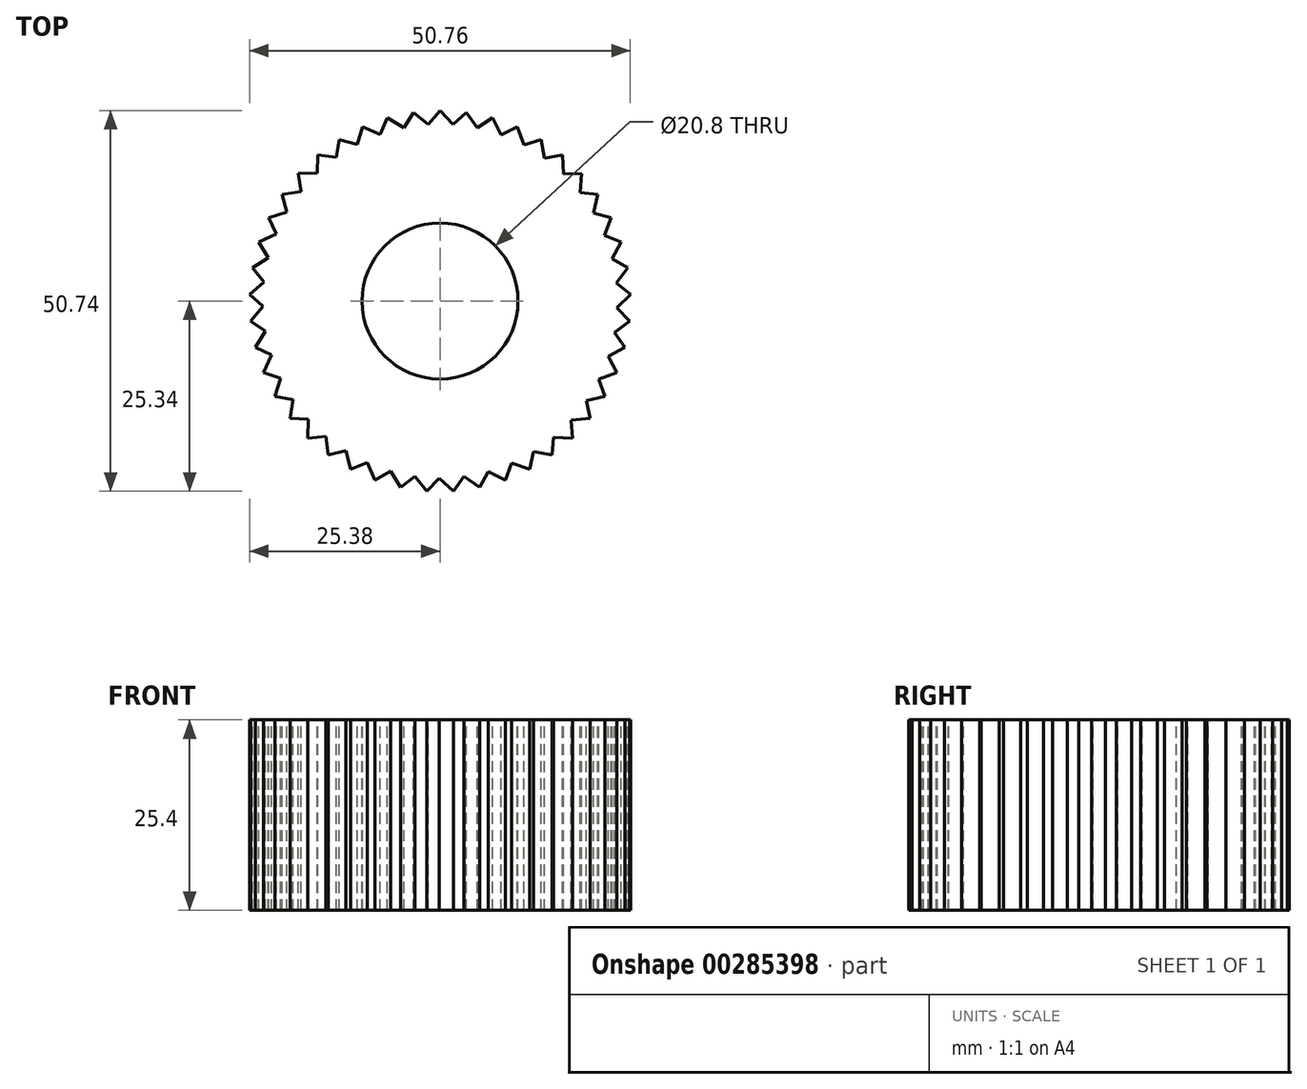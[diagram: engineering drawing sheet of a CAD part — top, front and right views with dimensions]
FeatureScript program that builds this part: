
annotation { "Feature Type Name" : "Feature", "Feature Type Description" : "" }
export const myFeature = defineFeature(function(context is Context, id is Id, definition is map)
    precondition{}
    {
        {
            var Q0;
            Q0=qCreatedBy(makeId("Top.planeOp"),FACE);
            var sketch = newSketch(context, id + "F0", { "sketchPlane" : qUnion([Q0])});
            skCircle(sketch, "E0", {"center": v(0, 0) * mm, "radius": 25.4 * mm});
            skSolve(sketch);
        }
        {
            var Q0;
            Q0=makeQuery(id+"F0.imprint","IMPRINT",FACE,{"disambiguationData":[TD([[makeQuery(id+"F0.imprint","IMPRINT",EDGE,{"derivedFrom":sQuery(id+"F0.wireOp",EDGE,"E0")}),1.0]])]});
            extrude(context, id + "F1", {"entities" : qUnion([Q0]), "depth" : 25.4 * mm});
        }
        {
            var Q0;
            Q0=makeQuery(id+"F1.opExtrude","CAP_FACE",FACE,{"disambiguationData":[OSD([sQuery(id+"F0.wireOp",EDGE,"E0")])],"isStart":false});
            var sketch = newSketch(context, id + "F2", { "sketchPlane" : qUnion([Q0])});
            skLineSegment(sketch, "E1", {"start": v(0, 0) * mm, "end": v(0, 49.68) * mm});
            skLineSegment(sketch, "E2", {"start": v(0, 24.84) * mm, "end": v(0, 25.4) * mm});
            skLineSegment(sketch, "E3", {"start": v(0, 25.4) * mm, "end": v(2.47, 22.76) * mm});
            skLineSegment(sketch, "E4", {"start": v(2.47, 22.76) * mm, "end": v(-2.23, 22.76) * mm});
            skLineSegment(sketch, "E5", {"start": v(-2.23, 22.76) * mm, "end": v(0, 25.4) * mm});
            skCircle(sketch, "E6.0", {"center": v(0, 0) * mm, "radius": 25.4 * mm});
            skLineSegment(sketch, "E7.1.1", {"start": v(-3.53, 25.15) * mm, "end": v(-0.72, 22.88) * mm});
            skLineSegment(sketch, "E7.1.2", {"start": v(-0.72, 22.88) * mm, "end": v(-5.38, 22.23) * mm});
            skLineSegment(sketch, "E7.1.3", {"start": v(-5.38, 22.23) * mm, "end": v(-3.53, 25.15) * mm});
            skLineSegment(sketch, "E7.2.1", {"start": v(-7, 24.42) * mm, "end": v(-3.9, 22.56) * mm});
            skLineSegment(sketch, "E7.2.2", {"start": v(-3.9, 22.56) * mm, "end": v(-8.42, 21.26) * mm});
            skLineSegment(sketch, "E7.2.3", {"start": v(-8.42, 21.26) * mm, "end": v(-7, 24.42) * mm});
            skLineSegment(sketch, "E8.2.3.0", {"start": v(-10.33, 23.2) * mm, "end": v(-7, 21.8) * mm});
            skLineSegment(sketch, "E8.5.3.0", {"start": v(-7, 21.8) * mm, "end": v(-11.3, 19.88) * mm});
            skLineSegment(sketch, "E8.8.3.0", {"start": v(-11.3, 19.88) * mm, "end": v(-10.33, 23.2) * mm});
            skLineSegment(sketch, "E8.2.4.0", {"start": v(-13.46, 21.54) * mm, "end": v(-9.96, 20.6) * mm});
            skLineSegment(sketch, "E8.5.4.0", {"start": v(-9.96, 20.6) * mm, "end": v(-13.96, 18.12) * mm});
            skLineSegment(sketch, "E8.8.4.0", {"start": v(-13.96, 18.12) * mm, "end": v(-13.46, 21.54) * mm});
            skLineSegment(sketch, "E8.2.5.0", {"start": v(-16.33, 19.46) * mm, "end": v(-12.74, 19.02) * mm});
            skLineSegment(sketch, "E8.5.5.0", {"start": v(-12.74, 19.02) * mm, "end": v(-16.34, 16) * mm});
            skLineSegment(sketch, "E8.8.5.0", {"start": v(-16.34, 16) * mm, "end": v(-16.33, 19.46) * mm});
            skLineSegment(sketch, "E8.2.6.0", {"start": v(-18.88, 17) * mm, "end": v(-15.26, 17.06) * mm});
            skLineSegment(sketch, "E8.5.6.0", {"start": v(-15.26, 17.06) * mm, "end": v(-18.4, 13.57) * mm});
            skLineSegment(sketch, "E8.8.6.0", {"start": v(-18.4, 13.57) * mm, "end": v(-18.88, 17) * mm});
            skLineSegment(sketch, "E8.2.7.0", {"start": v(-21.06, 14.2) * mm, "end": v(-17.49, 14.78) * mm});
            skLineSegment(sketch, "E8.5.7.0", {"start": v(-17.49, 14.78) * mm, "end": v(-20.12, 10.87) * mm});
            skLineSegment(sketch, "E8.8.7.0", {"start": v(-20.12, 10.87) * mm, "end": v(-21.06, 14.2) * mm});
            skLineSegment(sketch, "E8.2.8.0", {"start": v(-22.83, 11.13) * mm, "end": v(-19.37, 12.2) * mm});
            skLineSegment(sketch, "E8.5.8.0", {"start": v(-19.37, 12.2) * mm, "end": v(-21.43, 7.97) * mm});
            skLineSegment(sketch, "E8.8.8.0", {"start": v(-21.43, 7.97) * mm, "end": v(-22.83, 11.13) * mm});
            skLineSegment(sketch, "E8.2.9.0", {"start": v(-24.16, 7.85) * mm, "end": v(-20.88, 9.38) * mm});
            skLineSegment(sketch, "E8.5.9.0", {"start": v(-20.88, 9.38) * mm, "end": v(-22.34, 4.9) * mm});
            skLineSegment(sketch, "E8.8.9.0", {"start": v(-22.34, 4.9) * mm, "end": v(-24.16, 7.85) * mm});
            skLineSegment(sketch, "E8.2.10.0", {"start": v(-25.01, 4.41) * mm, "end": v(-21.98, 6.39) * mm});
            skLineSegment(sketch, "E8.5.10.0", {"start": v(-21.98, 6.39) * mm, "end": v(-22.8, 1.75) * mm});
            skLineSegment(sketch, "E8.8.10.0", {"start": v(-22.8, 1.75) * mm, "end": v(-25.01, 4.41) * mm});
            skLineSegment(sketch, "E8.2.11.0", {"start": v(-25.38, 0.89) * mm, "end": v(-22.66, 3.26) * mm});
            skLineSegment(sketch, "E8.5.11.0", {"start": v(-22.66, 3.26) * mm, "end": v(-22.82, -1.44) * mm});
            skLineSegment(sketch, "E8.8.11.0", {"start": v(-22.82, -1.44) * mm, "end": v(-25.38, 0.89) * mm});
            skLineSegment(sketch, "E8.2.12.0", {"start": v(-25.26, -2.66) * mm, "end": v(-22.9, 0.08) * mm});
            skLineSegment(sketch, "E8.5.12.0", {"start": v(-22.9, 0.08) * mm, "end": v(-22.4, -4.6) * mm});
            skLineSegment(sketch, "E8.8.12.0", {"start": v(-22.4, -4.6) * mm, "end": v(-25.26, -2.66) * mm});
            skLineSegment(sketch, "E8.2.13.0", {"start": v(-24.65, -6.14) * mm, "end": v(-22.68, -3.1) * mm});
            skLineSegment(sketch, "E8.5.13.0", {"start": v(-22.68, -3.1) * mm, "end": v(-21.54, -7.67) * mm});
            skLineSegment(sketch, "E8.8.13.0", {"start": v(-21.54, -7.67) * mm, "end": v(-24.65, -6.14) * mm});
            skLineSegment(sketch, "E8.2.14.0", {"start": v(-23.55, -9.52) * mm, "end": v(-22.03, -6.23) * mm});
            skLineSegment(sketch, "E8.5.14.0", {"start": v(-22.03, -6.23) * mm, "end": v(-20.26, -10.6) * mm});
            skLineSegment(sketch, "E8.8.14.0", {"start": v(-20.26, -10.6) * mm, "end": v(-23.55, -9.52) * mm});
            skLineSegment(sketch, "E8.2.15.0", {"start": v(-22, -12.7) * mm, "end": v(-20.95, -9.24) * mm});
            skLineSegment(sketch, "E8.5.15.0", {"start": v(-20.95, -9.24) * mm, "end": v(-18.6, -13.31) * mm});
            skLineSegment(sketch, "E8.8.15.0", {"start": v(-18.6, -13.31) * mm, "end": v(-22, -12.7) * mm});
            skLineSegment(sketch, "E8.2.16.0", {"start": v(-20.02, -15.64) * mm, "end": v(-19.46, -12.06) * mm});
            skLineSegment(sketch, "E8.5.16.0", {"start": v(-19.46, -12.06) * mm, "end": v(-16.56, -15.77) * mm});
            skLineSegment(sketch, "E8.8.16.0", {"start": v(-16.56, -15.77) * mm, "end": v(-20.02, -15.64) * mm});
            skLineSegment(sketch, "E8.2.17.0", {"start": v(-17.64, -18.27) * mm, "end": v(-17.59, -14.65) * mm});
            skLineSegment(sketch, "E8.5.17.0", {"start": v(-17.59, -14.65) * mm, "end": v(-14.2, -17.92) * mm});
            skLineSegment(sketch, "E8.8.17.0", {"start": v(-14.2, -17.92) * mm, "end": v(-17.64, -18.27) * mm});
            skLineSegment(sketch, "E8.2.18.0", {"start": v(-14.93, -20.55) * mm, "end": v(-15.38, -16.96) * mm});
            skLineSegment(sketch, "E8.5.18.0", {"start": v(-15.38, -16.96) * mm, "end": v(-11.57, -19.73) * mm});
            skLineSegment(sketch, "E8.8.18.0", {"start": v(-11.57, -19.73) * mm, "end": v(-14.93, -20.55) * mm});
            skLineSegment(sketch, "E8.2.19.0", {"start": v(-11.92, -22.43) * mm, "end": v(-12.87, -18.93) * mm});
            skLineSegment(sketch, "E8.5.19.0", {"start": v(-12.87, -18.93) * mm, "end": v(-8.71, -21.14) * mm});
            skLineSegment(sketch, "E8.8.19.0", {"start": v(-8.71, -21.14) * mm, "end": v(-11.92, -22.43) * mm});
            skLineSegment(sketch, "E8.2.20.0", {"start": v(-8.69, -23.87) * mm, "end": v(-10.1, -20.54) * mm});
            skLineSegment(sketch, "E8.5.20.0", {"start": v(-10.1, -20.54) * mm, "end": v(-5.68, -22.15) * mm});
            skLineSegment(sketch, "E8.8.20.0", {"start": v(-5.68, -22.15) * mm, "end": v(-8.69, -23.87) * mm});
            skLineSegment(sketch, "E8.2.21.0", {"start": v(-5.28, -24.84) * mm, "end": v(-7.15, -21.75) * mm});
            skLineSegment(sketch, "E8.5.21.0", {"start": v(-7.15, -21.75) * mm, "end": v(-2.55, -22.73) * mm});
            skLineSegment(sketch, "E8.8.21.0", {"start": v(-2.55, -22.73) * mm, "end": v(-5.28, -24.84) * mm});
            skLineSegment(sketch, "E8.2.22.0", {"start": v(-1.77, -25.34) * mm, "end": v(-4.05, -22.53) * mm});
            skLineSegment(sketch, "E8.5.22.0", {"start": v(-4.05, -22.53) * mm, "end": v(0.64, -22.86) * mm});
            skLineSegment(sketch, "E8.8.22.0", {"start": v(0.64, -22.86) * mm, "end": v(-1.77, -25.34) * mm});
            skLineSegment(sketch, "E8.2.23.0", {"start": v(1.77, -25.34) * mm, "end": v(-0.88, -22.88) * mm});
            skLineSegment(sketch, "E8.5.23.0", {"start": v(-0.88, -22.88) * mm, "end": v(3.82, -22.55) * mm});
            skLineSegment(sketch, "E8.8.23.0", {"start": v(3.82, -22.55) * mm, "end": v(1.77, -25.34) * mm});
            skLineSegment(sketch, "E8.2.24.0", {"start": v(5.28, -24.84) * mm, "end": v(2.31, -22.78) * mm});
            skLineSegment(sketch, "E8.5.24.0", {"start": v(2.31, -22.78) * mm, "end": v(6.92, -21.8) * mm});
            skLineSegment(sketch, "E8.8.24.0", {"start": v(6.92, -21.8) * mm, "end": v(5.28, -24.84) * mm});
            skLineSegment(sketch, "E8.2.25.0", {"start": v(8.69, -23.87) * mm, "end": v(5.46, -22.23) * mm});
            skLineSegment(sketch, "E8.5.25.0", {"start": v(5.46, -22.23) * mm, "end": v(9.88, -20.62) * mm});
            skLineSegment(sketch, "E8.8.25.0", {"start": v(9.88, -20.62) * mm, "end": v(8.69, -23.87) * mm});
            skLineSegment(sketch, "E8.2.26.0", {"start": v(11.92, -22.43) * mm, "end": v(8.5, -21.25) * mm});
            skLineSegment(sketch, "E8.5.26.0", {"start": v(8.5, -21.25) * mm, "end": v(12.66, -19.05) * mm});
            skLineSegment(sketch, "E8.8.26.0", {"start": v(12.66, -19.05) * mm, "end": v(11.92, -22.43) * mm});
            skLineSegment(sketch, "E8.2.27.0", {"start": v(14.93, -20.55) * mm, "end": v(11.38, -19.86) * mm});
            skLineSegment(sketch, "E8.5.27.0", {"start": v(11.38, -19.86) * mm, "end": v(15.19, -17.1) * mm});
            skLineSegment(sketch, "E8.8.27.0", {"start": v(15.19, -17.1) * mm, "end": v(14.93, -20.55) * mm});
            skLineSegment(sketch, "E8.2.28.0", {"start": v(17.64, -18.27) * mm, "end": v(14.03, -18.09) * mm});
            skLineSegment(sketch, "E8.5.28.0", {"start": v(14.03, -18.09) * mm, "end": v(17.42, -14.82) * mm});
            skLineSegment(sketch, "E8.8.28.0", {"start": v(17.42, -14.82) * mm, "end": v(17.64, -18.27) * mm});
            skLineSegment(sketch, "E8.2.29.0", {"start": v(20.02, -15.64) * mm, "end": v(16.41, -15.96) * mm});
            skLineSegment(sketch, "E8.5.29.0", {"start": v(16.41, -15.96) * mm, "end": v(19.3, -12.25) * mm});
            skLineSegment(sketch, "E8.8.29.0", {"start": v(19.3, -12.25) * mm, "end": v(20.02, -15.64) * mm});
            skLineSegment(sketch, "E8.2.30.0", {"start": v(22, -12.7) * mm, "end": v(18.47, -13.52) * mm});
            skLineSegment(sketch, "E8.5.30.0", {"start": v(18.47, -13.52) * mm, "end": v(20.83, -9.44) * mm});
            skLineSegment(sketch, "E8.8.30.0", {"start": v(20.83, -9.44) * mm, "end": v(22, -12.7) * mm});
            skLineSegment(sketch, "E8.2.31.0", {"start": v(23.55, -9.52) * mm, "end": v(20.18, -10.82) * mm});
            skLineSegment(sketch, "E8.5.31.0", {"start": v(20.18, -10.82) * mm, "end": v(21.94, -6.45) * mm});
            skLineSegment(sketch, "E8.8.31.0", {"start": v(21.94, -6.45) * mm, "end": v(23.55, -9.52) * mm});
            skLineSegment(sketch, "E8.2.32.0", {"start": v(24.65, -6.14) * mm, "end": v(21.48, -7.9) * mm});
            skLineSegment(sketch, "E8.5.32.0", {"start": v(21.48, -7.9) * mm, "end": v(22.62, -3.34) * mm});
            skLineSegment(sketch, "E8.8.32.0", {"start": v(22.62, -3.34) * mm, "end": v(24.65, -6.14) * mm});
            skLineSegment(sketch, "E8.2.33.0", {"start": v(25.26, -2.66) * mm, "end": v(22.38, -4.84) * mm});
            skLineSegment(sketch, "E8.5.33.0", {"start": v(22.38, -4.84) * mm, "end": v(22.87, -0.16) * mm});
            skLineSegment(sketch, "E8.8.33.0", {"start": v(22.87, -0.16) * mm, "end": v(25.26, -2.66) * mm});
            skLineSegment(sketch, "E8.2.34.0", {"start": v(25.38, 0.89) * mm, "end": v(22.83, -1.68) * mm});
            skLineSegment(sketch, "E8.5.34.0", {"start": v(22.83, -1.68) * mm, "end": v(22.67, 3.03) * mm});
            skLineSegment(sketch, "E8.8.34.0", {"start": v(22.67, 3.03) * mm, "end": v(25.38, 0.89) * mm});
            skLineSegment(sketch, "E8.2.35.0", {"start": v(25.01, 4.41) * mm, "end": v(22.84, 1.52) * mm});
            skLineSegment(sketch, "E8.5.35.0", {"start": v(22.84, 1.52) * mm, "end": v(22.02, 6.15) * mm});
            skLineSegment(sketch, "E8.8.35.0", {"start": v(22.02, 6.15) * mm, "end": v(25.01, 4.41) * mm});
            skLineSegment(sketch, "E8.2.36.0", {"start": v(24.16, 7.85) * mm, "end": v(22.4, 4.68) * mm});
            skLineSegment(sketch, "E8.5.36.0", {"start": v(22.4, 4.68) * mm, "end": v(20.95, 9.16) * mm});
            skLineSegment(sketch, "E8.8.36.0", {"start": v(20.95, 9.16) * mm, "end": v(24.16, 7.85) * mm});
            skLineSegment(sketch, "E8.2.37.0", {"start": v(22.83, 11.13) * mm, "end": v(21.54, 7.76) * mm});
            skLineSegment(sketch, "E8.5.37.0", {"start": v(21.54, 7.76) * mm, "end": v(19.48, 11.99) * mm});
            skLineSegment(sketch, "E8.8.37.0", {"start": v(19.48, 11.99) * mm, "end": v(22.83, 11.13) * mm});
            skLineSegment(sketch, "E8.2.38.0", {"start": v(21.06, 14.2) * mm, "end": v(20.25, 10.68) * mm});
            skLineSegment(sketch, "E8.5.38.0", {"start": v(20.25, 10.68) * mm, "end": v(17.62, 14.58) * mm});
            skLineSegment(sketch, "E8.8.38.0", {"start": v(17.62, 14.58) * mm, "end": v(21.06, 14.2) * mm});
            skLineSegment(sketch, "E8.2.39.0", {"start": v(18.88, 17) * mm, "end": v(18.57, 13.4) * mm});
            skLineSegment(sketch, "E8.5.39.0", {"start": v(18.57, 13.4) * mm, "end": v(15.42, 16.89) * mm});
            skLineSegment(sketch, "E8.8.39.0", {"start": v(15.42, 16.89) * mm, "end": v(18.88, 17) * mm});
            skLineSegment(sketch, "E8.2.40.0", {"start": v(16.33, 19.46) * mm, "end": v(16.52, 15.85) * mm});
            skLineSegment(sketch, "E8.5.40.0", {"start": v(16.52, 15.85) * mm, "end": v(12.92, 18.87) * mm});
            skLineSegment(sketch, "E8.8.40.0", {"start": v(12.92, 18.87) * mm, "end": v(16.33, 19.46) * mm});
            skLineSegment(sketch, "E8.2.41.0", {"start": v(13.46, 21.54) * mm, "end": v(14.16, 18) * mm});
            skLineSegment(sketch, "E8.5.41.0", {"start": v(14.16, 18) * mm, "end": v(10.17, 20.48) * mm});
            skLineSegment(sketch, "E8.8.41.0", {"start": v(10.17, 20.48) * mm, "end": v(13.46, 21.54) * mm});
            skLineSegment(sketch, "E8.2.42.0", {"start": v(10.33, 23.2) * mm, "end": v(11.51, 19.79) * mm});
            skLineSegment(sketch, "E8.5.42.0", {"start": v(11.51, 19.79) * mm, "end": v(7.22, 21.7) * mm});
            skLineSegment(sketch, "E8.8.42.0", {"start": v(7.22, 21.7) * mm, "end": v(10.33, 23.2) * mm});
            skLineSegment(sketch, "E8.2.43.0", {"start": v(7, 24.42) * mm, "end": v(8.65, 21.2) * mm});
            skLineSegment(sketch, "E8.5.43.0", {"start": v(8.65, 21.2) * mm, "end": v(4.12, 22.5) * mm});
            skLineSegment(sketch, "E8.8.43.0", {"start": v(4.12, 22.5) * mm, "end": v(7, 24.42) * mm});
            skLineSegment(sketch, "E8.2.44.0", {"start": v(3.53, 25.15) * mm, "end": v(5.61, 22.2) * mm});
            skLineSegment(sketch, "E8.5.44.0", {"start": v(5.61, 22.2) * mm, "end": v(0.95, 22.85) * mm});
            skLineSegment(sketch, "E8.8.44.0", {"start": v(0.95, 22.85) * mm, "end": v(3.53, 25.15) * mm});
            skCircle(sketch, "E9", {"center": v(0, 0) * mm, "radius": 10.4 * mm});
            skSolve(sketch);
        }
        {
            var Q0;
            {var subQ1=sQuery(id+"F2.wireOp",EDGE,"E8.8.21.0");var subQ3=sQuery(id+"F2.wireOp",EDGE,"E8.2.22.0");var subQ4=makeQuery(id+"F2.imprint","INTERSECT",VERTEX,{"derivedFrom":[subQ1,subQ3]});Q0=makeQuery(id+"F2.imprint","IMPRINT",FACE,{"disambiguationData":[TD([[makeQuery(id+"F2.imprint","IMPRINT",EDGE,{"disambiguationData":[TD([[subQ4,-1.0]])],"derivedFrom":subQ1}),1.0]])]});}
            var Q1;
            {var subQ1=sQuery(id+"F2.wireOp",EDGE,"E8.8.22.0");var subQ3=sQuery(id+"F2.wireOp",EDGE,"E8.2.23.0");var subQ4=makeQuery(id+"F2.imprint","INTERSECT",VERTEX,{"derivedFrom":[subQ1,subQ3]});Q1=makeQuery(id+"F2.imprint","IMPRINT",FACE,{"disambiguationData":[TD([[makeQuery(id+"F2.imprint","IMPRINT",EDGE,{"disambiguationData":[TD([[subQ4,-1.0]])],"derivedFrom":subQ1}),1.0]])]});}
            var Q2;
            {var subQ1=sQuery(id+"F2.wireOp",EDGE,"E8.8.23.0");var subQ3=sQuery(id+"F2.wireOp",EDGE,"E8.2.24.0");var subQ4=makeQuery(id+"F2.imprint","INTERSECT",VERTEX,{"derivedFrom":[subQ1,subQ3]});Q2=makeQuery(id+"F2.imprint","IMPRINT",FACE,{"disambiguationData":[TD([[makeQuery(id+"F2.imprint","IMPRINT",EDGE,{"disambiguationData":[TD([[subQ4,-1.0]])],"derivedFrom":subQ1}),1.0]])]});}
            var Q3;
            {var subQ1=sQuery(id+"F2.wireOp",EDGE,"E8.8.24.0");var subQ3=sQuery(id+"F2.wireOp",EDGE,"E8.2.25.0");var subQ4=makeQuery(id+"F2.imprint","INTERSECT",VERTEX,{"derivedFrom":[subQ1,subQ3]});Q3=makeQuery(id+"F2.imprint","IMPRINT",FACE,{"disambiguationData":[TD([[makeQuery(id+"F2.imprint","IMPRINT",EDGE,{"disambiguationData":[TD([[subQ4,-1.0]])],"derivedFrom":subQ1}),1.0]])]});}
            var Q4;
            {var subQ1=sQuery(id+"F2.wireOp",EDGE,"E8.8.25.0");var subQ3=sQuery(id+"F2.wireOp",EDGE,"E8.2.26.0");var subQ4=makeQuery(id+"F2.imprint","INTERSECT",VERTEX,{"derivedFrom":[subQ1,subQ3]});Q4=makeQuery(id+"F2.imprint","IMPRINT",FACE,{"disambiguationData":[TD([[makeQuery(id+"F2.imprint","IMPRINT",EDGE,{"disambiguationData":[TD([[subQ4,-1.0]])],"derivedFrom":subQ1}),1.0]])]});}
            var Q5;
            {var subQ1=sQuery(id+"F2.wireOp",EDGE,"E8.8.26.0");var subQ3=sQuery(id+"F2.wireOp",EDGE,"E8.2.27.0");var subQ4=makeQuery(id+"F2.imprint","INTERSECT",VERTEX,{"derivedFrom":[subQ1,subQ3]});Q5=makeQuery(id+"F2.imprint","IMPRINT",FACE,{"disambiguationData":[TD([[makeQuery(id+"F2.imprint","IMPRINT",EDGE,{"disambiguationData":[TD([[subQ4,-1.0]])],"derivedFrom":subQ1}),1.0]])]});}
            var Q6;
            {var subQ1=sQuery(id+"F2.wireOp",EDGE,"E8.8.27.0");var subQ3=sQuery(id+"F2.wireOp",EDGE,"E8.2.28.0");var subQ4=makeQuery(id+"F2.imprint","INTERSECT",VERTEX,{"derivedFrom":[subQ1,subQ3]});Q6=makeQuery(id+"F2.imprint","IMPRINT",FACE,{"disambiguationData":[TD([[makeQuery(id+"F2.imprint","IMPRINT",EDGE,{"disambiguationData":[TD([[subQ4,-1.0]])],"derivedFrom":subQ1}),1.0]])]});}
            var Q7;
            {var subQ1=sQuery(id+"F2.wireOp",EDGE,"E8.8.28.0");var subQ3=sQuery(id+"F2.wireOp",EDGE,"E8.2.29.0");var subQ4=makeQuery(id+"F2.imprint","INTERSECT",VERTEX,{"derivedFrom":[subQ1,subQ3]});Q7=makeQuery(id+"F2.imprint","IMPRINT",FACE,{"disambiguationData":[TD([[makeQuery(id+"F2.imprint","IMPRINT",EDGE,{"disambiguationData":[TD([[subQ4,-1.0]])],"derivedFrom":subQ1}),1.0]])]});}
            var Q8;
            {var subQ1=sQuery(id+"F2.wireOp",EDGE,"E8.8.29.0");var subQ3=sQuery(id+"F2.wireOp",EDGE,"E8.2.30.0");var subQ4=makeQuery(id+"F2.imprint","INTERSECT",VERTEX,{"derivedFrom":[subQ1,subQ3]});Q8=makeQuery(id+"F2.imprint","IMPRINT",FACE,{"disambiguationData":[TD([[makeQuery(id+"F2.imprint","IMPRINT",EDGE,{"disambiguationData":[TD([[subQ4,-1.0]])],"derivedFrom":subQ1}),1.0]])]});}
            var Q9;
            {var subQ1=sQuery(id+"F2.wireOp",EDGE,"E8.8.30.0");var subQ3=sQuery(id+"F2.wireOp",EDGE,"E8.2.31.0");var subQ4=makeQuery(id+"F2.imprint","INTERSECT",VERTEX,{"derivedFrom":[subQ1,subQ3]});Q9=makeQuery(id+"F2.imprint","IMPRINT",FACE,{"disambiguationData":[TD([[makeQuery(id+"F2.imprint","IMPRINT",EDGE,{"disambiguationData":[TD([[subQ4,-1.0]])],"derivedFrom":subQ1}),1.0]])]});}
            var Q10;
            {var subQ1=sQuery(id+"F2.wireOp",EDGE,"E8.8.31.0");var subQ3=sQuery(id+"F2.wireOp",EDGE,"E8.2.32.0");var subQ4=makeQuery(id+"F2.imprint","INTERSECT",VERTEX,{"derivedFrom":[subQ1,subQ3]});Q10=makeQuery(id+"F2.imprint","IMPRINT",FACE,{"disambiguationData":[TD([[makeQuery(id+"F2.imprint","IMPRINT",EDGE,{"disambiguationData":[TD([[subQ4,-1.0]])],"derivedFrom":subQ1}),1.0]])]});}
            var Q11;
            {var subQ1=sQuery(id+"F2.wireOp",EDGE,"E8.8.32.0");var subQ3=sQuery(id+"F2.wireOp",EDGE,"E8.2.33.0");var subQ4=makeQuery(id+"F2.imprint","INTERSECT",VERTEX,{"derivedFrom":[subQ1,subQ3]});Q11=makeQuery(id+"F2.imprint","IMPRINT",FACE,{"disambiguationData":[TD([[makeQuery(id+"F2.imprint","IMPRINT",EDGE,{"disambiguationData":[TD([[subQ4,-1.0]])],"derivedFrom":subQ1}),1.0]])]});}
            var Q12;
            {var subQ1=sQuery(id+"F2.wireOp",EDGE,"E8.8.33.0");var subQ3=sQuery(id+"F2.wireOp",EDGE,"E8.2.34.0");var subQ4=makeQuery(id+"F2.imprint","INTERSECT",VERTEX,{"derivedFrom":[subQ1,subQ3]});Q12=makeQuery(id+"F2.imprint","IMPRINT",FACE,{"disambiguationData":[TD([[makeQuery(id+"F2.imprint","IMPRINT",EDGE,{"disambiguationData":[TD([[subQ4,-1.0]])],"derivedFrom":subQ1}),1.0]])]});}
            var Q13;
            {var subQ1=sQuery(id+"F2.wireOp",EDGE,"E8.8.34.0");var subQ3=sQuery(id+"F2.wireOp",EDGE,"E8.2.35.0");var subQ4=makeQuery(id+"F2.imprint","INTERSECT",VERTEX,{"derivedFrom":[subQ1,subQ3]});Q13=makeQuery(id+"F2.imprint","IMPRINT",FACE,{"disambiguationData":[TD([[makeQuery(id+"F2.imprint","IMPRINT",EDGE,{"disambiguationData":[TD([[subQ4,-1.0]])],"derivedFrom":subQ1}),1.0]])]});}
            var Q14;
            {var subQ1=sQuery(id+"F2.wireOp",EDGE,"E8.8.35.0");var subQ3=sQuery(id+"F2.wireOp",EDGE,"E8.2.36.0");var subQ4=makeQuery(id+"F2.imprint","INTERSECT",VERTEX,{"derivedFrom":[subQ1,subQ3]});Q14=makeQuery(id+"F2.imprint","IMPRINT",FACE,{"disambiguationData":[TD([[makeQuery(id+"F2.imprint","IMPRINT",EDGE,{"disambiguationData":[TD([[subQ4,-1.0]])],"derivedFrom":subQ1}),1.0]])]});}
            var Q15;
            {var subQ1=sQuery(id+"F2.wireOp",EDGE,"E8.8.36.0");var subQ3=sQuery(id+"F2.wireOp",EDGE,"E8.2.37.0");var subQ4=makeQuery(id+"F2.imprint","INTERSECT",VERTEX,{"derivedFrom":[subQ1,subQ3]});Q15=makeQuery(id+"F2.imprint","IMPRINT",FACE,{"disambiguationData":[TD([[makeQuery(id+"F2.imprint","IMPRINT",EDGE,{"disambiguationData":[TD([[subQ4,-1.0]])],"derivedFrom":subQ1}),1.0]])]});}
            var Q16;
            {var subQ1=sQuery(id+"F2.wireOp",EDGE,"E8.8.37.0");var subQ3=sQuery(id+"F2.wireOp",EDGE,"E8.2.38.0");var subQ4=makeQuery(id+"F2.imprint","INTERSECT",VERTEX,{"derivedFrom":[subQ1,subQ3]});Q16=makeQuery(id+"F2.imprint","IMPRINT",FACE,{"disambiguationData":[TD([[makeQuery(id+"F2.imprint","IMPRINT",EDGE,{"disambiguationData":[TD([[subQ4,-1.0]])],"derivedFrom":subQ1}),1.0]])]});}
            var Q17;
            {var subQ1=sQuery(id+"F2.wireOp",EDGE,"E8.8.38.0");var subQ3=sQuery(id+"F2.wireOp",EDGE,"E8.2.39.0");var subQ4=makeQuery(id+"F2.imprint","INTERSECT",VERTEX,{"derivedFrom":[subQ1,subQ3]});Q17=makeQuery(id+"F2.imprint","IMPRINT",FACE,{"disambiguationData":[TD([[makeQuery(id+"F2.imprint","IMPRINT",EDGE,{"disambiguationData":[TD([[subQ4,-1.0]])],"derivedFrom":subQ1}),1.0]])]});}
            var Q18;
            {var subQ1=sQuery(id+"F2.wireOp",EDGE,"E8.8.39.0");var subQ3=sQuery(id+"F2.wireOp",EDGE,"E8.2.40.0");var subQ4=makeQuery(id+"F2.imprint","INTERSECT",VERTEX,{"derivedFrom":[subQ1,subQ3]});Q18=makeQuery(id+"F2.imprint","IMPRINT",FACE,{"disambiguationData":[TD([[makeQuery(id+"F2.imprint","IMPRINT",EDGE,{"disambiguationData":[TD([[subQ4,-1.0]])],"derivedFrom":subQ1}),1.0]])]});}
            var Q19;
            {var subQ1=sQuery(id+"F2.wireOp",EDGE,"E8.8.40.0");var subQ3=sQuery(id+"F2.wireOp",EDGE,"E8.2.41.0");var subQ4=makeQuery(id+"F2.imprint","INTERSECT",VERTEX,{"derivedFrom":[subQ1,subQ3]});Q19=makeQuery(id+"F2.imprint","IMPRINT",FACE,{"disambiguationData":[TD([[makeQuery(id+"F2.imprint","IMPRINT",EDGE,{"disambiguationData":[TD([[subQ4,-1.0]])],"derivedFrom":subQ1}),1.0]])]});}
            var Q20;
            {var subQ1=sQuery(id+"F2.wireOp",EDGE,"E8.8.41.0");var subQ3=sQuery(id+"F2.wireOp",EDGE,"E8.2.42.0");var subQ4=makeQuery(id+"F2.imprint","INTERSECT",VERTEX,{"derivedFrom":[subQ1,subQ3]});Q20=makeQuery(id+"F2.imprint","IMPRINT",FACE,{"disambiguationData":[TD([[makeQuery(id+"F2.imprint","IMPRINT",EDGE,{"disambiguationData":[TD([[subQ4,-1.0]])],"derivedFrom":subQ1}),1.0]])]});}
            var Q21;
            {var subQ1=sQuery(id+"F2.wireOp",EDGE,"E8.8.42.0");var subQ3=sQuery(id+"F2.wireOp",EDGE,"E8.2.43.0");var subQ4=makeQuery(id+"F2.imprint","INTERSECT",VERTEX,{"derivedFrom":[subQ1,subQ3]});Q21=makeQuery(id+"F2.imprint","IMPRINT",FACE,{"disambiguationData":[TD([[makeQuery(id+"F2.imprint","IMPRINT",EDGE,{"disambiguationData":[TD([[subQ4,-1.0]])],"derivedFrom":subQ1}),1.0]])]});}
            var Q22;
            {var subQ1=sQuery(id+"F2.wireOp",EDGE,"E8.8.43.0");var subQ3=sQuery(id+"F2.wireOp",EDGE,"E8.2.44.0");var subQ4=makeQuery(id+"F2.imprint","INTERSECT",VERTEX,{"derivedFrom":[subQ1,subQ3]});Q22=makeQuery(id+"F2.imprint","IMPRINT",FACE,{"disambiguationData":[TD([[makeQuery(id+"F2.imprint","IMPRINT",EDGE,{"disambiguationData":[TD([[subQ4,-1.0]])],"derivedFrom":subQ1}),1.0]])]});}
            var Q23;
            {var subQ1=sQuery(id+"F2.wireOp",EDGE,"E3");var subQ3=sQuery(id+"F2.wireOp",EDGE,"E8.8.44.0");var subQ4=makeQuery(id+"F2.imprint","INTERSECT",VERTEX,{"derivedFrom":[subQ1,subQ3]});Q23=makeQuery(id+"F2.imprint","IMPRINT",FACE,{"disambiguationData":[TD([[makeQuery(id+"F2.imprint","IMPRINT",EDGE,{"disambiguationData":[TD([[subQ4,-1.0]])],"derivedFrom":subQ3}),1.0]])]});}
            var Q24;
            {var subQ1=sQuery(id+"F2.wireOp",EDGE,"E5");var subQ3=sQuery(id+"F2.wireOp",EDGE,"E7.1.1");var subQ4=makeQuery(id+"F2.imprint","INTERSECT",VERTEX,{"derivedFrom":[subQ1,subQ3]});Q24=makeQuery(id+"F2.imprint","IMPRINT",FACE,{"disambiguationData":[TD([[makeQuery(id+"F2.imprint","IMPRINT",EDGE,{"disambiguationData":[TD([[subQ4,1.0]])],"derivedFrom":subQ3}),1.0]])]});}
            var Q25;
            {var subQ1=sQuery(id+"F2.wireOp",EDGE,"E7.1.3");var subQ3=sQuery(id+"F2.wireOp",EDGE,"E7.2.1");var subQ4=makeQuery(id+"F2.imprint","INTERSECT",VERTEX,{"derivedFrom":[subQ1,subQ3]});Q25=makeQuery(id+"F2.imprint","IMPRINT",FACE,{"disambiguationData":[TD([[makeQuery(id+"F2.imprint","IMPRINT",EDGE,{"disambiguationData":[TD([[subQ4,-1.0]])],"derivedFrom":subQ1}),1.0]])]});}
            var Q26;
            {var subQ1=sQuery(id+"F2.wireOp",EDGE,"E7.2.3");var subQ3=sQuery(id+"F2.wireOp",EDGE,"E8.2.3.0");var subQ4=makeQuery(id+"F2.imprint","INTERSECT",VERTEX,{"derivedFrom":[subQ1,subQ3]});Q26=makeQuery(id+"F2.imprint","IMPRINT",FACE,{"disambiguationData":[TD([[makeQuery(id+"F2.imprint","IMPRINT",EDGE,{"disambiguationData":[TD([[subQ4,-1.0]])],"derivedFrom":subQ1}),1.0]])]});}
            var Q27;
            {var subQ1=sQuery(id+"F2.wireOp",EDGE,"E8.8.3.0");var subQ3=sQuery(id+"F2.wireOp",EDGE,"E8.2.4.0");var subQ4=makeQuery(id+"F2.imprint","INTERSECT",VERTEX,{"derivedFrom":[subQ1,subQ3]});Q27=makeQuery(id+"F2.imprint","IMPRINT",FACE,{"disambiguationData":[TD([[makeQuery(id+"F2.imprint","IMPRINT",EDGE,{"disambiguationData":[TD([[subQ4,-1.0]])],"derivedFrom":subQ1}),1.0]])]});}
            var Q28;
            {var subQ1=sQuery(id+"F2.wireOp",EDGE,"E8.8.4.0");var subQ3=sQuery(id+"F2.wireOp",EDGE,"E8.2.5.0");var subQ4=makeQuery(id+"F2.imprint","INTERSECT",VERTEX,{"derivedFrom":[subQ1,subQ3]});Q28=makeQuery(id+"F2.imprint","IMPRINT",FACE,{"disambiguationData":[TD([[makeQuery(id+"F2.imprint","IMPRINT",EDGE,{"disambiguationData":[TD([[subQ4,-1.0]])],"derivedFrom":subQ1}),1.0]])]});}
            var Q29;
            {var subQ1=sQuery(id+"F2.wireOp",EDGE,"E8.8.5.0");var subQ3=sQuery(id+"F2.wireOp",EDGE,"E8.2.6.0");var subQ4=makeQuery(id+"F2.imprint","INTERSECT",VERTEX,{"derivedFrom":[subQ1,subQ3]});Q29=makeQuery(id+"F2.imprint","IMPRINT",FACE,{"disambiguationData":[TD([[makeQuery(id+"F2.imprint","IMPRINT",EDGE,{"disambiguationData":[TD([[subQ4,-1.0]])],"derivedFrom":subQ1}),1.0]])]});}
            var Q30;
            {var subQ1=sQuery(id+"F2.wireOp",EDGE,"E8.8.6.0");var subQ3=sQuery(id+"F2.wireOp",EDGE,"E8.2.7.0");var subQ4=makeQuery(id+"F2.imprint","INTERSECT",VERTEX,{"derivedFrom":[subQ1,subQ3]});Q30=makeQuery(id+"F2.imprint","IMPRINT",FACE,{"disambiguationData":[TD([[makeQuery(id+"F2.imprint","IMPRINT",EDGE,{"disambiguationData":[TD([[subQ4,-1.0]])],"derivedFrom":subQ1}),1.0]])]});}
            var Q31;
            {var subQ1=sQuery(id+"F2.wireOp",EDGE,"E8.8.7.0");var subQ3=sQuery(id+"F2.wireOp",EDGE,"E8.2.8.0");var subQ4=makeQuery(id+"F2.imprint","INTERSECT",VERTEX,{"derivedFrom":[subQ1,subQ3]});Q31=makeQuery(id+"F2.imprint","IMPRINT",FACE,{"disambiguationData":[TD([[makeQuery(id+"F2.imprint","IMPRINT",EDGE,{"disambiguationData":[TD([[subQ4,-1.0]])],"derivedFrom":subQ1}),1.0]])]});}
            var Q32;
            {var subQ1=sQuery(id+"F2.wireOp",EDGE,"E8.8.8.0");var subQ3=sQuery(id+"F2.wireOp",EDGE,"E8.2.9.0");var subQ4=makeQuery(id+"F2.imprint","INTERSECT",VERTEX,{"derivedFrom":[subQ1,subQ3]});Q32=makeQuery(id+"F2.imprint","IMPRINT",FACE,{"disambiguationData":[TD([[makeQuery(id+"F2.imprint","IMPRINT",EDGE,{"disambiguationData":[TD([[subQ4,-1.0]])],"derivedFrom":subQ1}),1.0]])]});}
            var Q33;
            {var subQ1=sQuery(id+"F2.wireOp",EDGE,"E8.8.9.0");var subQ3=sQuery(id+"F2.wireOp",EDGE,"E8.2.10.0");var subQ4=makeQuery(id+"F2.imprint","INTERSECT",VERTEX,{"derivedFrom":[subQ1,subQ3]});Q33=makeQuery(id+"F2.imprint","IMPRINT",FACE,{"disambiguationData":[TD([[makeQuery(id+"F2.imprint","IMPRINT",EDGE,{"disambiguationData":[TD([[subQ4,-1.0]])],"derivedFrom":subQ1}),1.0]])]});}
            var Q34;
            {var subQ1=sQuery(id+"F2.wireOp",EDGE,"E8.8.10.0");var subQ3=sQuery(id+"F2.wireOp",EDGE,"E8.2.11.0");var subQ4=makeQuery(id+"F2.imprint","INTERSECT",VERTEX,{"derivedFrom":[subQ1,subQ3]});Q34=makeQuery(id+"F2.imprint","IMPRINT",FACE,{"disambiguationData":[TD([[makeQuery(id+"F2.imprint","IMPRINT",EDGE,{"disambiguationData":[TD([[subQ4,-1.0]])],"derivedFrom":subQ1}),1.0]])]});}
            var Q35;
            {var subQ1=sQuery(id+"F2.wireOp",EDGE,"E8.8.11.0");var subQ3=sQuery(id+"F2.wireOp",EDGE,"E8.2.12.0");var subQ4=makeQuery(id+"F2.imprint","INTERSECT",VERTEX,{"derivedFrom":[subQ1,subQ3]});Q35=makeQuery(id+"F2.imprint","IMPRINT",FACE,{"disambiguationData":[TD([[makeQuery(id+"F2.imprint","IMPRINT",EDGE,{"disambiguationData":[TD([[subQ4,-1.0]])],"derivedFrom":subQ1}),1.0]])]});}
            var Q36;
            {var subQ1=sQuery(id+"F2.wireOp",EDGE,"E8.8.12.0");var subQ3=sQuery(id+"F2.wireOp",EDGE,"E8.2.13.0");var subQ4=makeQuery(id+"F2.imprint","INTERSECT",VERTEX,{"derivedFrom":[subQ1,subQ3]});Q36=makeQuery(id+"F2.imprint","IMPRINT",FACE,{"disambiguationData":[TD([[makeQuery(id+"F2.imprint","IMPRINT",EDGE,{"disambiguationData":[TD([[subQ4,-1.0]])],"derivedFrom":subQ1}),1.0]])]});}
            var Q37;
            {var subQ1=sQuery(id+"F2.wireOp",EDGE,"E8.8.13.0");var subQ3=sQuery(id+"F2.wireOp",EDGE,"E8.2.14.0");var subQ4=makeQuery(id+"F2.imprint","INTERSECT",VERTEX,{"derivedFrom":[subQ1,subQ3]});Q37=makeQuery(id+"F2.imprint","IMPRINT",FACE,{"disambiguationData":[TD([[makeQuery(id+"F2.imprint","IMPRINT",EDGE,{"disambiguationData":[TD([[subQ4,-1.0]])],"derivedFrom":subQ1}),1.0]])]});}
            var Q38;
            {var subQ1=sQuery(id+"F2.wireOp",EDGE,"E8.8.14.0");var subQ3=sQuery(id+"F2.wireOp",EDGE,"E8.2.15.0");var subQ4=makeQuery(id+"F2.imprint","INTERSECT",VERTEX,{"derivedFrom":[subQ1,subQ3]});Q38=makeQuery(id+"F2.imprint","IMPRINT",FACE,{"disambiguationData":[TD([[makeQuery(id+"F2.imprint","IMPRINT",EDGE,{"disambiguationData":[TD([[subQ4,-1.0]])],"derivedFrom":subQ1}),1.0]])]});}
            var Q39;
            {var subQ1=sQuery(id+"F2.wireOp",EDGE,"E8.8.15.0");var subQ3=sQuery(id+"F2.wireOp",EDGE,"E8.2.16.0");var subQ4=makeQuery(id+"F2.imprint","INTERSECT",VERTEX,{"derivedFrom":[subQ1,subQ3]});Q39=makeQuery(id+"F2.imprint","IMPRINT",FACE,{"disambiguationData":[TD([[makeQuery(id+"F2.imprint","IMPRINT",EDGE,{"disambiguationData":[TD([[subQ4,-1.0]])],"derivedFrom":subQ1}),1.0]])]});}
            var Q40;
            {var subQ1=sQuery(id+"F2.wireOp",EDGE,"E8.8.16.0");var subQ3=sQuery(id+"F2.wireOp",EDGE,"E8.2.17.0");var subQ4=makeQuery(id+"F2.imprint","INTERSECT",VERTEX,{"derivedFrom":[subQ1,subQ3]});Q40=makeQuery(id+"F2.imprint","IMPRINT",FACE,{"disambiguationData":[TD([[makeQuery(id+"F2.imprint","IMPRINT",EDGE,{"disambiguationData":[TD([[subQ4,-1.0]])],"derivedFrom":subQ1}),1.0]])]});}
            var Q41;
            {var subQ1=sQuery(id+"F2.wireOp",EDGE,"E8.8.17.0");var subQ3=sQuery(id+"F2.wireOp",EDGE,"E8.2.18.0");var subQ4=makeQuery(id+"F2.imprint","INTERSECT",VERTEX,{"derivedFrom":[subQ1,subQ3]});Q41=makeQuery(id+"F2.imprint","IMPRINT",FACE,{"disambiguationData":[TD([[makeQuery(id+"F2.imprint","IMPRINT",EDGE,{"disambiguationData":[TD([[subQ4,-1.0]])],"derivedFrom":subQ1}),1.0]])]});}
            var Q42;
            {var subQ1=sQuery(id+"F2.wireOp",EDGE,"E8.8.18.0");var subQ3=sQuery(id+"F2.wireOp",EDGE,"E8.2.19.0");var subQ4=makeQuery(id+"F2.imprint","INTERSECT",VERTEX,{"derivedFrom":[subQ1,subQ3]});Q42=makeQuery(id+"F2.imprint","IMPRINT",FACE,{"disambiguationData":[TD([[makeQuery(id+"F2.imprint","IMPRINT",EDGE,{"disambiguationData":[TD([[subQ4,-1.0]])],"derivedFrom":subQ1}),1.0]])]});}
            var Q43;
            {var subQ1=sQuery(id+"F2.wireOp",EDGE,"E8.8.19.0");var subQ3=sQuery(id+"F2.wireOp",EDGE,"E8.2.20.0");var subQ4=makeQuery(id+"F2.imprint","INTERSECT",VERTEX,{"derivedFrom":[subQ1,subQ3]});Q43=makeQuery(id+"F2.imprint","IMPRINT",FACE,{"disambiguationData":[TD([[makeQuery(id+"F2.imprint","IMPRINT",EDGE,{"disambiguationData":[TD([[subQ4,-1.0]])],"derivedFrom":subQ1}),1.0]])]});}
            var Q44;
            {var subQ1=sQuery(id+"F2.wireOp",EDGE,"E8.8.20.0");var subQ3=sQuery(id+"F2.wireOp",EDGE,"E8.2.21.0");var subQ4=makeQuery(id+"F2.imprint","INTERSECT",VERTEX,{"derivedFrom":[subQ1,subQ3]});Q44=makeQuery(id+"F2.imprint","IMPRINT",FACE,{"disambiguationData":[TD([[makeQuery(id+"F2.imprint","IMPRINT",EDGE,{"disambiguationData":[TD([[subQ4,-1.0]])],"derivedFrom":subQ1}),1.0]])]});}
            extrude(context, id + "F3", {"entities" : qUnion([Q0, Q1, Q2, Q3, Q4, Q5, Q6, Q7, Q8, Q9, Q10, Q11, Q12, Q13, Q14, Q15, Q16, Q17, Q18, Q19, Q20, Q21, Q22, Q23, Q24, Q25, Q26, Q27, Q28, Q29, Q30, Q31, Q32, Q33, Q34, Q35, Q36, Q37, Q38, Q39, Q40, Q41, Q42, Q43, Q44]), "operationType" : NewBodyOperationType.REMOVE, "oppositeDirection" : true, "depth" : 25.4 * mm});
        }
        {
            var Q0;
            Q0=makeQuery(id+"F2.imprint","IMPRINT",FACE,{"disambiguationData":[TD([[makeQuery(id+"F2.imprint","IMPRINT",EDGE,{"derivedFrom":sQuery(id+"F2.wireOp",EDGE,"E9")}),1.0]])]});
            extrude(context, id + "F4", {"entities" : qUnion([Q0]), "operationType" : NewBodyOperationType.REMOVE, "oppositeDirection" : true, "depth" : 25.4 * mm});
        }
    });
